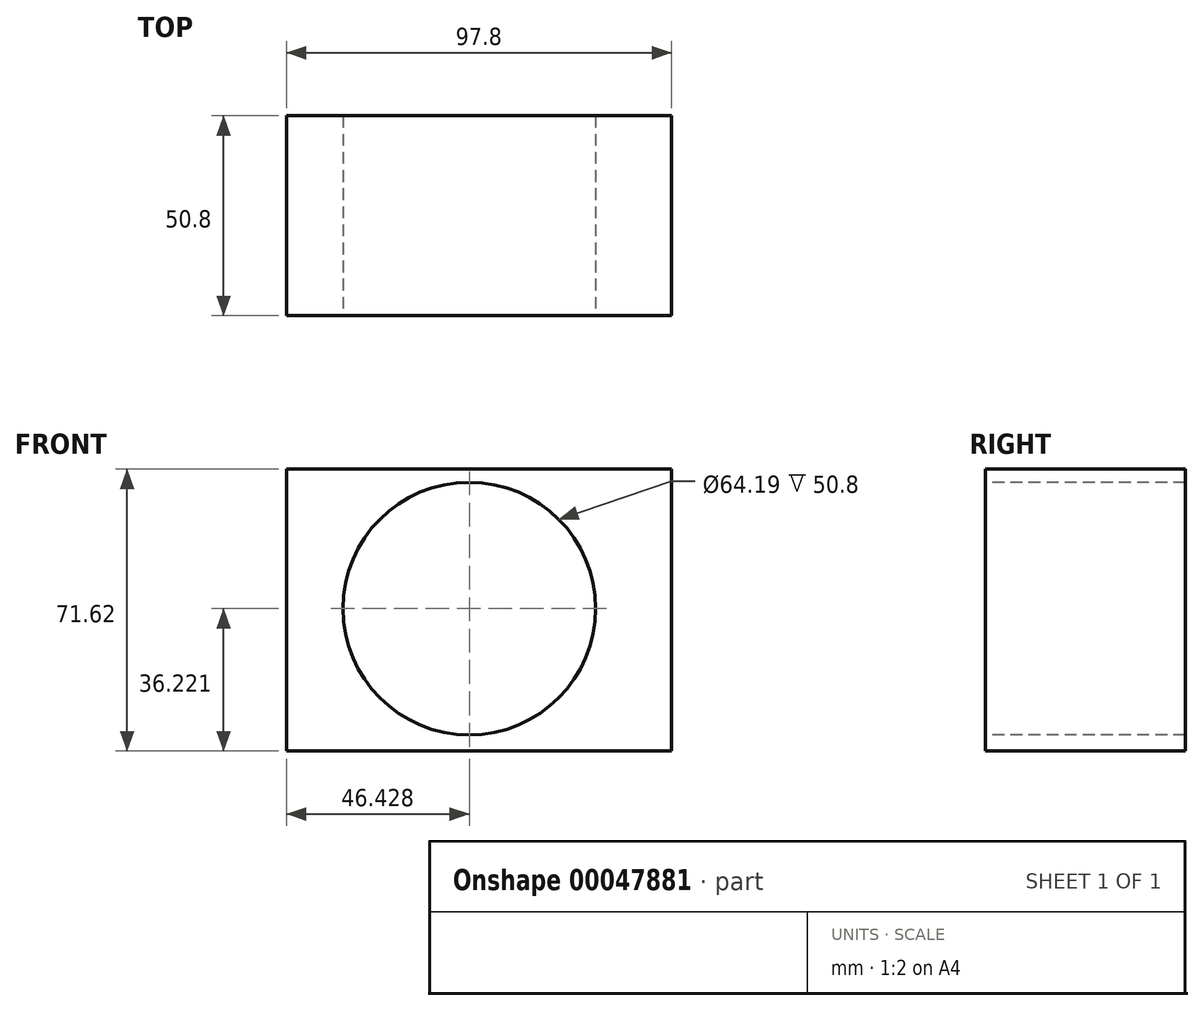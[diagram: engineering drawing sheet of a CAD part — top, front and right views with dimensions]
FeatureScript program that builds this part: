
annotation { "Feature Type Name" : "Feature", "Feature Type Description" : "" }
export const myFeature = defineFeature(function(context is Context, id is Id, definition is map)
    precondition{}
    {
        {
            var Q0;
            Q0=qCreatedBy(makeId("Front.planeOp"),FACE);
            var sketch = newSketch(context, id + "F0", { "sketchPlane" : qUnion([Q0])});
            skLineSegment(sketch, "E0.rect.bottom", {"start": v(-18.8, 7.4) * mm, "end": v(-116.6, 7.4) * mm});
            skLineSegment(sketch, "E0.rect.top", {"start": v(-18.8, 79.01) * mm, "end": v(-116.6, 79.01) * mm});
            skLineSegment(sketch, "E0.rect.left", {"start": v(-18.8, 7.4) * mm, "end": v(-18.8, 79.01) * mm});
            skLineSegment(sketch, "E0.rect.right", {"start": v(-116.6, 7.4) * mm, "end": v(-116.6, 79.01) * mm});
            skPoint(sketch, "E0.rect.middle", {"position": v(-67.7, 43.2) * mm});
            skSolve(sketch);
        }
        {
            var Q0;
            Q0=makeQuery(id+"F0.imprint","IMPRINT",FACE,{"disambiguationData":[TD([[makeQuery(id+"F0.imprint","IMPRINT",EDGE,{"derivedFrom":sQuery(id+"F0.wireOp",EDGE,"E0.rect.bottom")}),-1.0]])]});
            extrude(context, id + "F1", {"entities" : qUnion([Q0]), "depth" : 50.8 * mm});
        }
        {
            var Q0;
            Q0=makeQuery(id+"F1.opExtrude","CAP_FACE",FACE,{"disambiguationData":[OSD([sQuery(id+"F0.wireOp",EDGE,"E0.rect.bottom"),sQuery(id+"F0.wireOp",EDGE,"E0.rect.top"),sQuery(id+"F0.wireOp",EDGE,"E0.rect.left"),sQuery(id+"F0.wireOp",EDGE,"E0.rect.right")])],"isStart":false});
            var sketch = newSketch(context, id + "F2", { "sketchPlane" : qUnion([Q0])});
            skCircle(sketch, "E1", {"center": v(-70.18, 43.61) * mm, "radius": 32.1 * mm});
            skSolve(sketch);
        }
        {
            var Q0;
            Q0 = qSketchRegion(id + "F2", true);
            var Q1;
            Q1=makeQuery(id+"F2.imprint","IMPRINT",FACE,{"disambiguationData":[TD([[makeQuery(id+"F2.imprint","IMPRINT",EDGE,{"derivedFrom":sQuery(id+"F2.wireOp",EDGE,"E1")}),1.0]])]});
            extrude(context, id + "F3", {"entities" : qUnion([Q0, Q1]), "operationType" : NewBodyOperationType.REMOVE, "endBound" : BoundingType.THROUGH_ALL, "oppositeDirection" : true, "depth" : 25.4 * mm});
        }
    });
